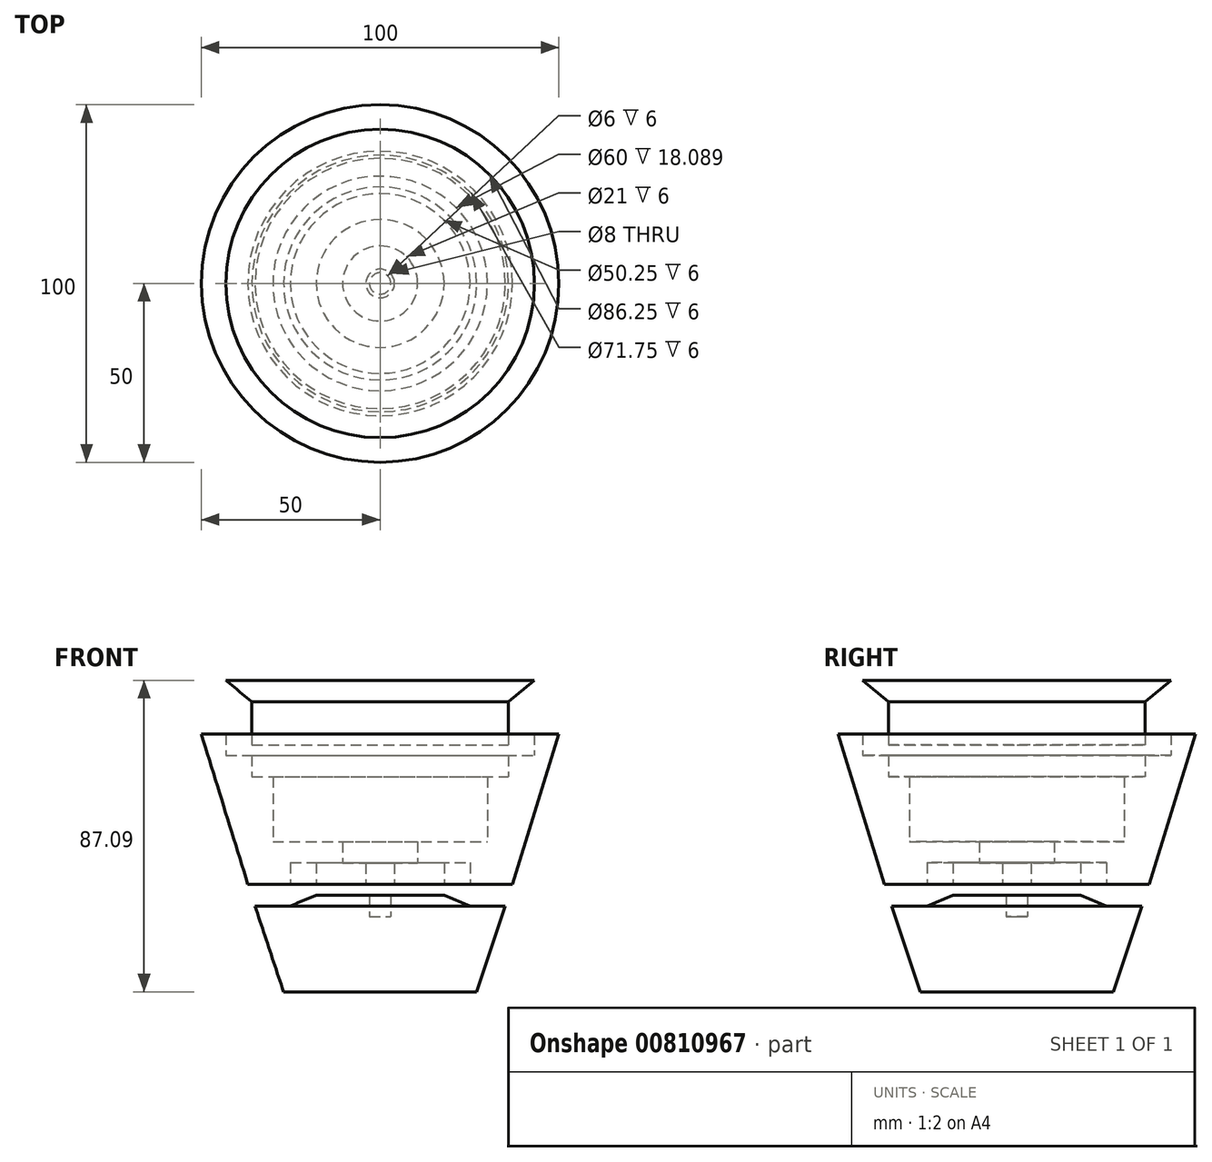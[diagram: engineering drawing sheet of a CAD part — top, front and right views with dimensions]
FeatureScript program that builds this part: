
annotation { "Feature Type Name" : "Feature", "Feature Type Description" : "" }
export const myFeature = defineFeature(function(context is Context, id is Id, definition is map)
    precondition{}
    {
        {
            var Q0;
            Q0=qCreatedBy(makeId("Front.planeOp"),FACE);
            var sketch = newSketch(context, id + "F0", { "sketchPlane" : qUnion([Q0])});
            skLineSegment(sketch, "E0", {"start": v(0, 0) * mm, "end": v(27, 0) * mm});
            skLineSegment(sketch, "E1", {"start": v(27, 0) * mm, "end": v(35, 24) * mm});
            skLineSegment(sketch, "E2", {"start": v(3, 21) * mm, "end": v(0, 21) * mm});
            skLineSegment(sketch, "E3", {"start": v(0, 21) * mm, "end": v(0, 0) * mm});
            skLineSegment(sketch, "E4", {"start": v(17.87, 30.09) * mm, "end": v(17.87, 36.09) * mm});
            skLineSegment(sketch, "E5", {"start": v(17.87, 36.09) * mm, "end": v(25.12, 36.09) * mm});
            skLineSegment(sketch, "E6", {"start": v(25.12, 36.09) * mm, "end": v(25.12, 30.09) * mm});
            skLineSegment(sketch, "E7", {"start": v(3, 27) * mm, "end": v(17.87, 27) * mm});
            skLineSegment(sketch, "E8", {"start": v(17.87, 27) * mm, "end": v(25.12, 24) * mm});
            skLineSegment(sketch, "E9", {"start": v(25.12, 24) * mm, "end": v(35, 24) * mm});
            skLineSegment(sketch, "E10", {"start": v(25.12, 30.09) * mm, "end": v(37, 30.09) * mm});
            skLineSegment(sketch, "E11", {"start": v(4, 30) * mm, "end": v(4, 36) * mm});
            skLineSegment(sketch, "E12", {"start": v(4, 36) * mm, "end": v(10.5, 36) * mm});
            skLineSegment(sketch, "E13", {"start": v(10.5, 36) * mm, "end": v(10.5, 42) * mm});
            skLineSegment(sketch, "E14", {"start": v(10.5, 42) * mm, "end": v(30, 42) * mm});
            skLineSegment(sketch, "E15", {"start": v(30, 42) * mm, "end": v(30, 60.09) * mm});
            skLineSegment(sketch, "E16", {"start": v(30, 60.09) * mm, "end": v(35.87, 60.09) * mm});
            skLineSegment(sketch, "E17", {"start": v(35.87, 60.09) * mm, "end": v(35.87, 66.09) * mm});
            skLineSegment(sketch, "E18", {"start": v(35.87, 66.09) * mm, "end": v(43.12, 66.09) * mm});
            skLineSegment(sketch, "E19", {"start": v(43.12, 66.09) * mm, "end": v(43.12, 72.09) * mm});
            skLineSegment(sketch, "E20", {"start": v(43.12, 72.09) * mm, "end": v(50, 72.09) * mm});
            skLineSegment(sketch, "E21", {"start": v(50, 72.09) * mm, "end": v(37, 30.09) * mm});
            skLineSegment(sketch, "E22", {"start": v(17.87, 30.09) * mm, "end": v(4, 30) * mm});
            skLineSegment(sketch, "E23", {"start": v(35.87, 69.09) * mm, "end": v(0, 69.09) * mm});
            skLineSegment(sketch, "E24", {"start": v(0, 69.09) * mm, "end": v(0, 87.09) * mm});
            skLineSegment(sketch, "E25", {"start": v(0, 87.09) * mm, "end": v(43.12, 87.09) * mm});
            skLineSegment(sketch, "E26", {"start": v(43.12, 87.09) * mm, "end": v(35.87, 81.09) * mm});
            skLineSegment(sketch, "E27", {"start": v(35.87, 81.09) * mm, "end": v(35.87, 69.09) * mm});
            skLineSegment(sketch, "E28", {"start": v(3, 27) * mm, "end": v(3, 21) * mm});
            skSolve(sketch);
        }
        {
            var Q0;
            Q0 = qSketchRegion(id + "F0", true);
            var Q1;
            Q1=sQuery(id+"F0.wireOp",EDGE,"E24");
            revolve(context, id + "F1", {"surfaceOperationType" : NewSurfaceOperationType.NEW, "entities" : qUnion([Q0]), "axis" : qUnion([Q1]), "revolveType" : RevolveType.FULL});
        }
    });
